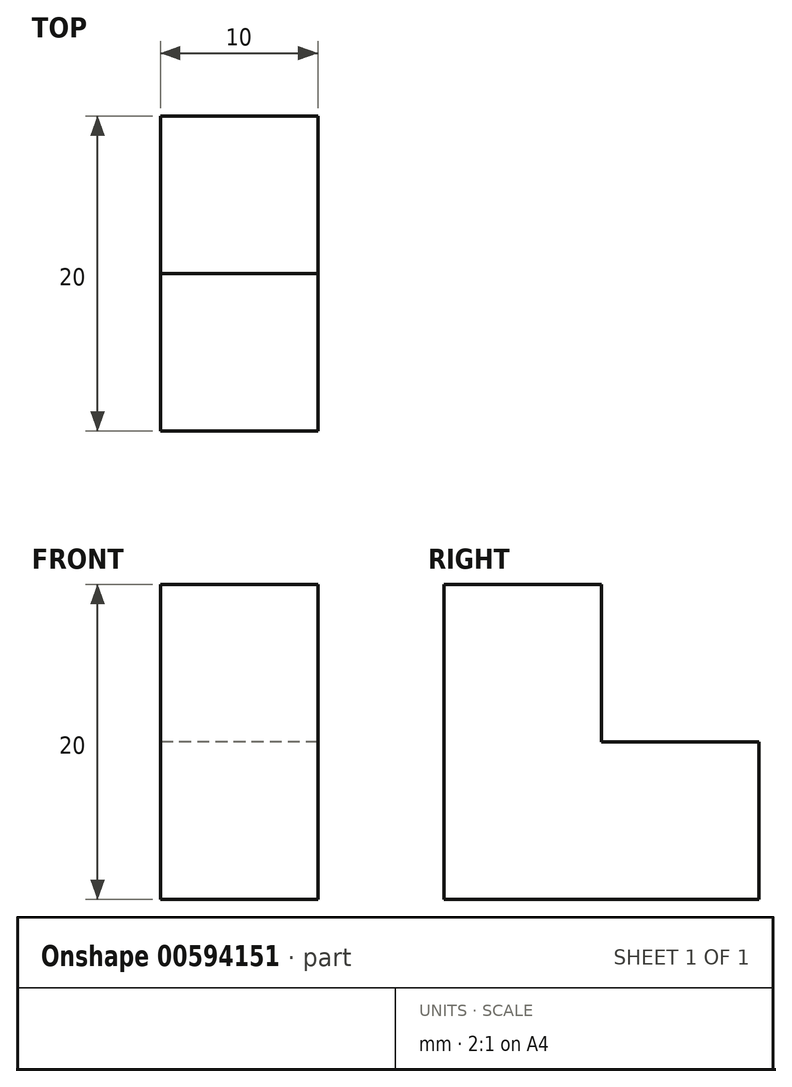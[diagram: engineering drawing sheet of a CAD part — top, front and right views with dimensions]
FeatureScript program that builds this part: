
annotation { "Feature Type Name" : "Feature", "Feature Type Description" : "" }
export const myFeature = defineFeature(function(context is Context, id is Id, definition is map)
    precondition{}
    {
        {
            var Q0;
            Q0=qCreatedBy(makeId("Right.planeOp"),FACE);
            var sketch = newSketch(context, id + "F0", { "sketchPlane" : qUnion([Q0])});
            skLineSegment(sketch, "E0", {"start": v(0, 0) * mm, "end": v(0, 20) * mm});
            skLineSegment(sketch, "E1", {"start": v(0, 20) * mm, "end": v(10, 20) * mm});
            skLineSegment(sketch, "E2", {"start": v(10, 20) * mm, "end": v(10, 10) * mm});
            skLineSegment(sketch, "E3", {"start": v(10, 10) * mm, "end": v(20, 10) * mm});
            skLineSegment(sketch, "E4", {"start": v(20, 10) * mm, "end": v(20, 0) * mm});
            skLineSegment(sketch, "E5", {"start": v(20, 0) * mm, "end": v(0, 0) * mm});
            skSolve(sketch);
        }
        {
            var Q0;
            Q0=makeQuery(id+"F0.imprint","IMPRINT",FACE,{"disambiguationData":[TD([[makeQuery(id+"F0.imprint","IMPRINT",EDGE,{"derivedFrom":sQuery(id+"F0.wireOp",EDGE,"E0")}),-1.0]])]});
            extrude(context, id + "F1", {"entities" : qUnion([Q0]), "depth" : 10 * mm, "offsetDistance" : 25 * mm});
        }
    });
